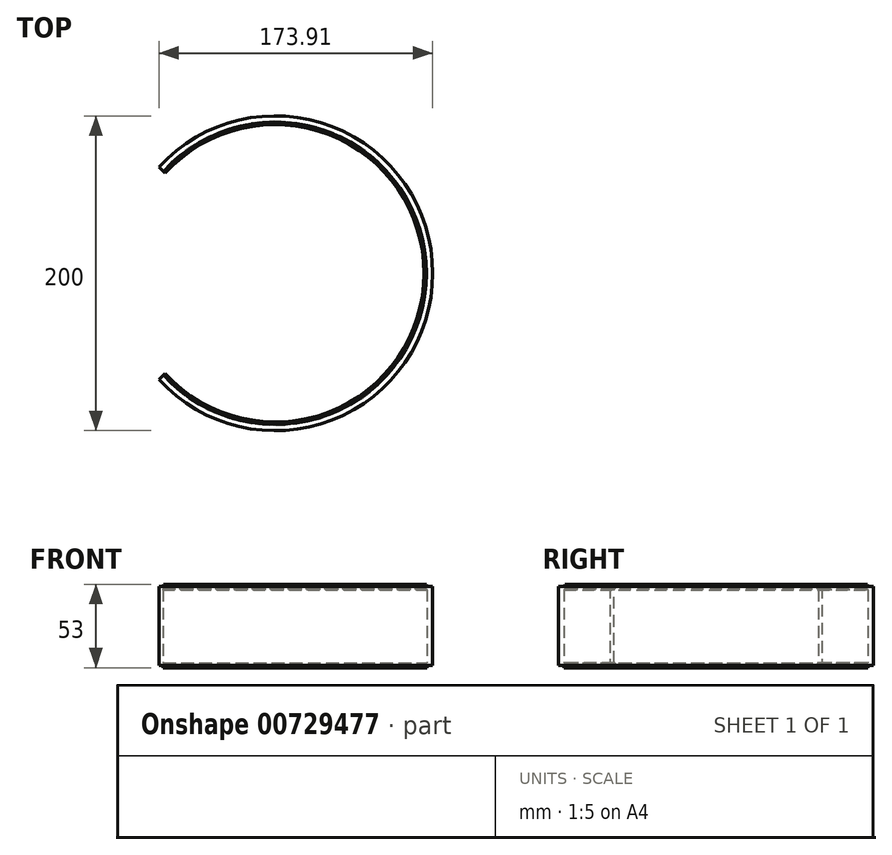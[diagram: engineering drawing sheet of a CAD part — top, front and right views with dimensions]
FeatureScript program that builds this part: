
annotation { "Feature Type Name" : "Feature", "Feature Type Description" : "" }
export const myFeature = defineFeature(function(context is Context, id is Id, definition is map)
    precondition{}
    {
        {
            var Q0;
            Q0=qCreatedBy(makeId("Top.planeOp"),FACE);
            var sketch = newSketch(context, id + "F0", { "sketchPlane" : qUnion([Q0])});
            skCircle(sketch, "E0", {"center": v(0, 0) * mm, "radius": 96.5 * mm});
            skCircle(sketch, "E1.0", {"center": v(0, 0) * mm, "radius": 100 * mm});
            skLineSegment(sketch, "E2", {"start": v(-61.2, 0) * mm, "end": v(64.12, 0) * mm, "construction": true});
            skLineSegment(sketch, "E3", {"start": v(0, 57.07) * mm, "end": v(0, -66.3) * mm, "construction": true});
            skPoint(sketch, "E4", {"position": v(-71.32, 65) * mm});
            skPoint(sketch, "E5", {"position": v(-71.32, -65) * mm});
            skLineSegment(sketch, "E6", {"start": v(-71.32, 65) * mm, "end": v(-73.91, 67.36) * mm});
            skLineSegment(sketch, "E7", {"start": v(-71.32, -65) * mm, "end": v(-73.91, -67.36) * mm});
            skCircle(sketch, "E8", {"center": v(0, 0) * mm, "radius": 95.5 * mm});
            skLineSegment(sketch, "E9", {"start": v(-71.32, 65) * mm, "end": v(-70.59, 64.33) * mm});
            skLineSegment(sketch, "E10", {"start": v(-71.32, -65) * mm, "end": v(-70.59, -64.33) * mm});
            skSolve(sketch);
        }
        {
            var Q0;
            {var subQ0=sQuery(id+"F0.wireOp",EDGE,"E6");Q0=makeQuery(id+"F0.imprint","IMPRINT",FACE,{"disambiguationData":[TD([[makeQuery(id+"F0.imprint","IMPRINT",EDGE,{"derivedFrom":subQ0}),-1.0]])]});}
            extrude(context, id + "F1", {"entities" : qUnion([Q0]), "depth" : 50 * mm, "offsetDistance" : 25 * mm});
        }
        {
            var Q0;
            {var subQ0=sQuery(id+"F0.wireOp",EDGE,"E9");Q0=makeQuery(id+"F0.imprint","IMPRINT",FACE,{"disambiguationData":[TD([[makeQuery(id+"F0.imprint","IMPRINT",EDGE,{"derivedFrom":subQ0}),1.0]])]});}
            extrude(context, id + "F2", {"entities" : qUnion([Q0]), "operationType" : NewBodyOperationType.ADD, "endBound" : BoundingType.SYMMETRIC, "depth" : 3 * mm, "offsetDistance" : 25 * mm});
        }
        {
            var Q0;
            Q0=makeQuery(id+"F1.opExtrude","CAP_FACE",FACE,{"disambiguationData":[OSD([sQuery(id+"F0.wireOp",EDGE,"E0"),sQuery(id+"F0.wireOp",EDGE,"E1.0"),sQuery(id+"F0.wireOp",EDGE,"E6"),sQuery(id+"F0.wireOp",EDGE,"E7")])],"isStart":false});
            var sketch = newSketch(context, id + "F3", { "sketchPlane" : qUnion([Q0])});
            skCircle(sketch, "E11", {"center": v(0, 0) * mm, "radius": 100 * mm});
            skCircle(sketch, "E12", {"center": v(0, 0) * mm, "radius": 96.5 * mm});
            skCircle(sketch, "E13", {"center": v(0, 0) * mm, "radius": 94.5 * mm});
            skCircle(sketch, "E14", {"center": v(0, 0) * mm, "radius": 96 * mm});
            skLineSegment(sketch, "E15", {"start": v(-71.33, -65) * mm, "end": v(-70.96, -64.66) * mm});
            skLineSegment(sketch, "E16", {"start": v(-70.96, -64.66) * mm, "end": v(-69.86, -63.63) * mm});
            skLineSegment(sketch, "E17", {"start": v(-69.86, -63.63) * mm, "end": v(-69.86, -63.63) * mm});
            skLineSegment(sketch, "E18", {"start": v(-71.33, 65) * mm, "end": v(-70.97, 64.65) * mm});
            skLineSegment(sketch, "E19", {"start": v(-70.97, 64.65) * mm, "end": v(-69.83, 63.67) * mm});
            skSolve(sketch);
        }
        {
            var Q0;
            {var subQ3=sQuery(id+"F3.wireOp",EDGE,"E15");Q0=makeQuery(id+"F3.imprint","IMPRINT",FACE,{"disambiguationData":[TD([[makeQuery(id+"F3.imprint","IMPRINT",EDGE,{"derivedFrom":subQ3}),-1.0]])]});}
            extrude(context, id + "F4", {"entities" : qUnion([Q0]), "operationType" : NewBodyOperationType.ADD, "oppositeDirection" : true, "depth" : 2 * mm, "offsetDistance" : 25 * mm});
        }
        {
            var Q0;
            {var subQ0=sQuery(id+"F3.wireOp",EDGE,"E16");Q0=makeQuery(id+"F3.imprint","IMPRINT",FACE,{"disambiguationData":[TD([[makeQuery(id+"F3.imprint","IMPRINT",EDGE,{"derivedFrom":subQ0}),-1.0]])]});}
            extrude(context, id + "F5", {"entities" : qUnion([Q0]), "operationType" : NewBodyOperationType.ADD, "endBound" : BoundingType.SYMMETRIC, "depth" : 3 * mm, "offsetDistance" : 25 * mm});
        }
        {
            var Q0;
            Q0=makeQuery(id+"F5.opExtrude","CAP_EDGE",EDGE,{"disambiguationData":[OSD([sQuery(id+"F3.wireOp",EDGE,"E13")])],"isStart":true});
            chamfer(context, id + "F6", {"entities" : qUnion([Q0]), "width" : 1.4 * mm, "tangentPropagation" : true});
        }
        {
            var Q0;
            Q0=makeQuery(id+"F4.opExtrude","CAP_EDGE",EDGE,{"disambiguationData":[OSD([sQuery(id+"F3.wireOp",EDGE,"E14")])],"isStart":false});
            chamfer(context, id + "F7", {"entities" : qUnion([Q0]), "width" : 0.5 * mm, "tangentPropagation" : true});
        }
    });
